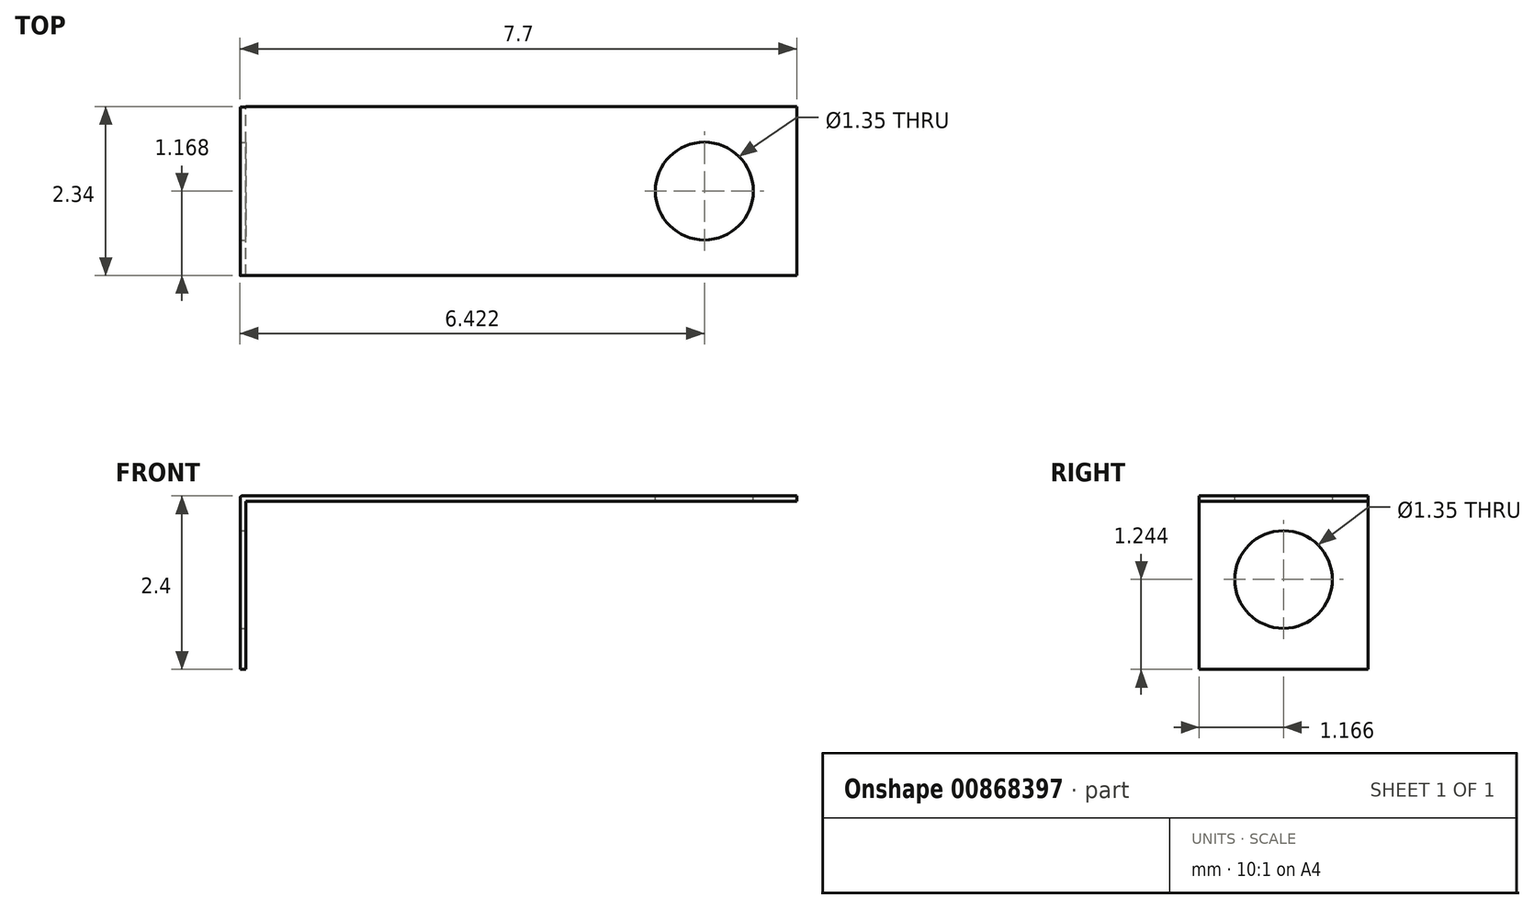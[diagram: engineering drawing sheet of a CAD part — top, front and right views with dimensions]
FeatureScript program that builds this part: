
annotation { "Feature Type Name" : "Feature", "Feature Type Description" : "" }
export const myFeature = defineFeature(function(context is Context, id is Id, definition is map)
    precondition{}
    {
        {
            var Q0;
            Q0=qCreatedBy(makeId("Top.planeOp"),FACE);
            var sketch = newSketch(context, id + "F0", { "sketchPlane" : qUnion([Q0])});
            skLineSegment(sketch, "E0.bottom", {"start": v(0, 0) * mm, "end": v(7.62, 0) * mm});
            skLineSegment(sketch, "E0.top", {"start": v(0, 2.34) * mm, "end": v(7.62, 2.34) * mm});
            skLineSegment(sketch, "E0.left", {"start": v(0, 0) * mm, "end": v(0, 2.34) * mm});
            skLineSegment(sketch, "E0.right", {"start": v(7.62, 0) * mm, "end": v(7.62, 2.34) * mm});
            skLineSegment(sketch, "E1", {"start": v(0, 1.17) * mm, "end": v(6.34, 1.17) * mm});
            skCircle(sketch, "E2", {"center": v(6.34, 1.17) * mm, "radius": 0.68 * mm});
            skSolve(sketch);
        }
        {
            var Q0;
            Q0=qCreatedBy(makeId("Right.planeOp"),FACE);
            var sketch = newSketch(context, id + "F1", { "sketchPlane" : qUnion([Q0])});
            skLineSegment(sketch, "E3.bottom", {"start": v(0, 0) * mm, "end": v(2.33, 0) * mm});
            skLineSegment(sketch, "E3.top", {"start": v(0, -2.4) * mm, "end": v(2.33, -2.4) * mm});
            skLineSegment(sketch, "E3.left", {"start": v(0, 0) * mm, "end": v(0, -2.4) * mm});
            skLineSegment(sketch, "E3.right", {"start": v(2.33, 0) * mm, "end": v(2.33, -2.4) * mm});
            skLineSegment(sketch, "E4", {"start": v(1.17, 0) * mm, "end": v(1.17, -1.16) * mm});
            skCircle(sketch, "E5", {"center": v(1.17, -1.16) * mm, "radius": 0.68 * mm});
            skSolve(sketch);
        }
        {
            var Q0;
            Q0 = qSketchRegion(id + "F1", true);
            extrude(context, id + "F2", {"entities" : qUnion([Q0]), "oppositeDirection" : true, "depth" : 0.08 * mm, "offsetDistance" : 25.4 * mm});
        }
        {
            var Q0;
            Q0 = qSketchRegion(id + "F0", true);
            extrude(context, id + "F3", {"entities" : qUnion([Q0]), "operationType" : NewBodyOperationType.ADD, "oppositeDirection" : true, "depth" : 0.08 * mm, "offsetDistance" : 25.4 * mm});
        }
        {
            var Q0;
            Q0=makeQuery(id+"F2.opExtrude","CAP_EDGE",EDGE,{"disambiguationData":[OSD([sQuery(id+"F1.wireOp",EDGE,"E3.bottom")])],"isStart":false});
            fillet(context, id + "F4", {"entities" : qUnion([Q0]), "radius" : 0.03 * mm, "tangentPropagation" : true, "allowEdgeOverflow" : false});
        }
    });
